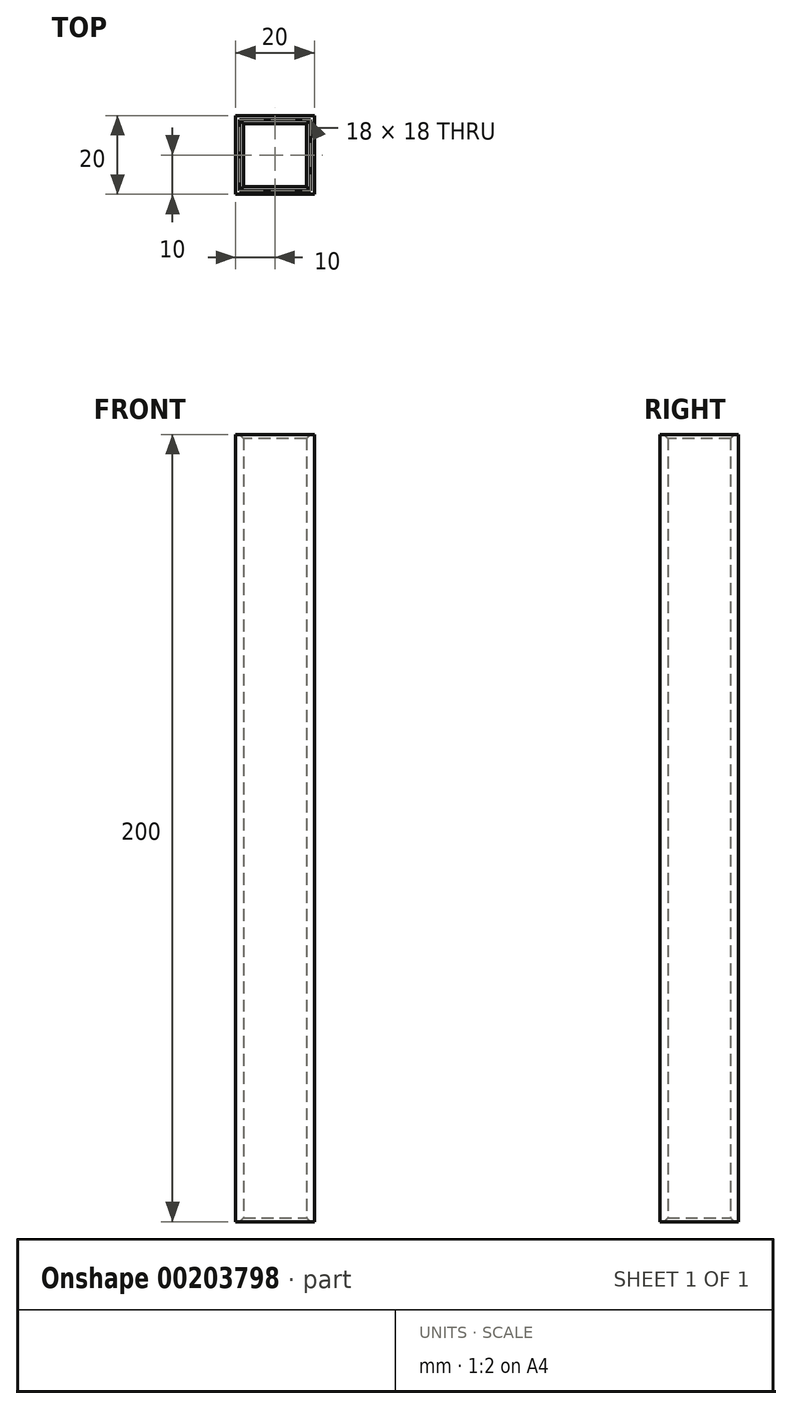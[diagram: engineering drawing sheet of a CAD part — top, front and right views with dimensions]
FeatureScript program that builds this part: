
annotation { "Feature Type Name" : "Feature", "Feature Type Description" : "" }
export const myFeature = defineFeature(function(context is Context, id is Id, definition is map)
    precondition{}
    {
        {
            var Q0;
            Q0=qCreatedBy(makeId("Top.planeOp"),FACE);
            var sketch = newSketch(context, id + "F0", { "sketchPlane" : qUnion([Q0])});
            skLineSegment(sketch, "E0.bottom", {"start": v(-10, 10) * mm, "end": v(10, 10) * mm});
            skLineSegment(sketch, "E0.top", {"start": v(-10, -10) * mm, "end": v(10, -10) * mm});
            skLineSegment(sketch, "E0.left", {"start": v(-10, 10) * mm, "end": v(-10, -10) * mm});
            skLineSegment(sketch, "E0.right", {"start": v(10, 10) * mm, "end": v(10, -10) * mm});
            skPoint(sketch, "E0.middle", {"position": v(0, 0) * mm});
            skLineSegment(sketch, "E1.0", {"start": v(-8, 8) * mm, "end": v(8, 8) * mm});
            skLineSegment(sketch, "E1.1", {"start": v(-8, 8) * mm, "end": v(-8, -8) * mm});
            skLineSegment(sketch, "E1.2", {"start": v(-8, -8) * mm, "end": v(8, -8) * mm});
            skLineSegment(sketch, "E1.3", {"start": v(8, 8) * mm, "end": v(8, -8) * mm});
            skSolve(sketch);
        }
        {
            var Q0;
            Q0=makeQuery(id+"F0.imprint","IMPRINT",FACE,{"disambiguationData":[TD([[makeQuery(id+"F0.imprint","IMPRINT",EDGE,{"derivedFrom":sQuery(id+"F0.wireOp",EDGE,"E0.bottom")}),-1.0]])]});
            extrude(context, id + "F1", {"entities" : qUnion([Q0]), "depth" : 200 * mm, "symmetric" : true});
        }
        {
            var Q0;
            Q0=makeQuery(id+"F1.opExtrude","CAP_EDGE",EDGE,{"disambiguationData":[OSD([sQuery(id+"F0.wireOp",EDGE,"E1.0")])],"isStart":false});
            var Q1;
            Q1=makeQuery(id+"F1.opExtrude","CAP_EDGE",EDGE,{"disambiguationData":[OSD([sQuery(id+"F0.wireOp",EDGE,"E1.1")])],"isStart":false});
            var Q2;
            Q2=makeQuery(id+"F1.opExtrude","CAP_EDGE",EDGE,{"disambiguationData":[OSD([sQuery(id+"F0.wireOp",EDGE,"E1.3")])],"isStart":false});
            var Q3;
            Q3=makeQuery(id+"F1.opExtrude","CAP_EDGE",EDGE,{"disambiguationData":[OSD([sQuery(id+"F0.wireOp",EDGE,"E1.2")])],"isStart":false});
            var Q4;
            Q4=makeQuery(id+"F1.opExtrude","CAP_EDGE",EDGE,{"disambiguationData":[OSD([sQuery(id+"F0.wireOp",EDGE,"E1.0")])],"isStart":true});
            var Q5;
            Q5=makeQuery(id+"F1.opExtrude","CAP_EDGE",EDGE,{"disambiguationData":[OSD([sQuery(id+"F0.wireOp",EDGE,"E1.3")])],"isStart":true});
            var Q6;
            Q6=makeQuery(id+"F1.opExtrude","CAP_EDGE",EDGE,{"disambiguationData":[OSD([sQuery(id+"F0.wireOp",EDGE,"E1.2")])],"isStart":true});
            var Q7;
            Q7=makeQuery(id+"F1.opExtrude","CAP_EDGE",EDGE,{"disambiguationData":[OSD([sQuery(id+"F0.wireOp",EDGE,"E1.1")])],"isStart":true});
            chamfer(context, id + "F2", {"entities" : qUnion([Q0, Q1, Q2, Q3, Q4, Q5, Q6, Q7]), "width" : 1 * mm, "tangentPropagation" : true});
        }
    });
